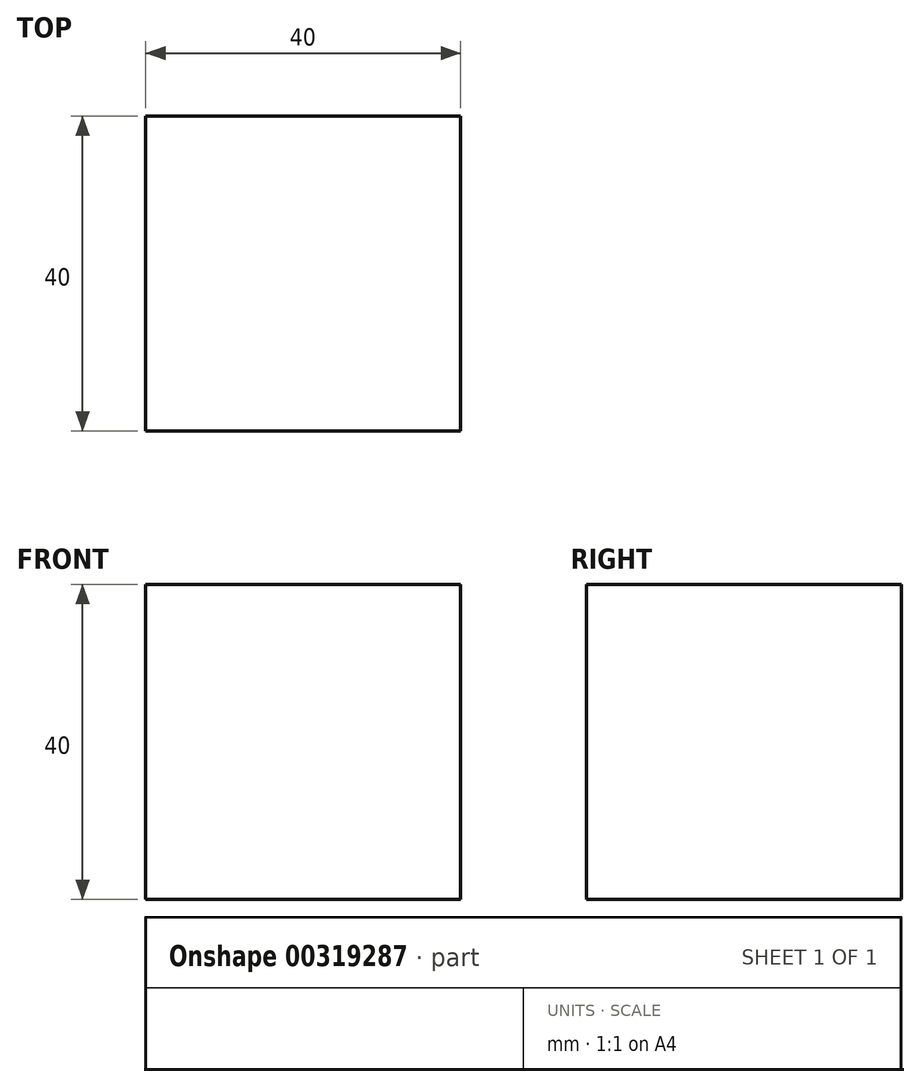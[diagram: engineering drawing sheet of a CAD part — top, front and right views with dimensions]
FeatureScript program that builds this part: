
annotation { "Feature Type Name" : "Feature", "Feature Type Description" : "" }
export const myFeature = defineFeature(function(context is Context, id is Id, definition is map)
    precondition{}
    {
        {
            var Q0;
            Q0=qCreatedBy(makeId("Front.planeOp"),FACE);
            var sketch = newSketch(context, id + "F0", { "sketchPlane" : qUnion([Q0])});
            skLineSegment(sketch, "E0.bottom", {"start": v(0, 0) * mm, "end": v(40, 0) * mm});
            skLineSegment(sketch, "E0.top", {"start": v(0, 40) * mm, "end": v(40, 40) * mm});
            skLineSegment(sketch, "E0.left", {"start": v(0, 0) * mm, "end": v(0, 40) * mm});
            skLineSegment(sketch, "E0.right", {"start": v(40, 0) * mm, "end": v(40, 40) * mm});
            skSolve(sketch);
        }
        {
            var Q0;
            Q0 = qSketchRegion(id + "F0", true);
            extrude(context, id + "F1", {"entities" : qUnion([Q0]), "depth" : 40 * mm});
        }
    });
